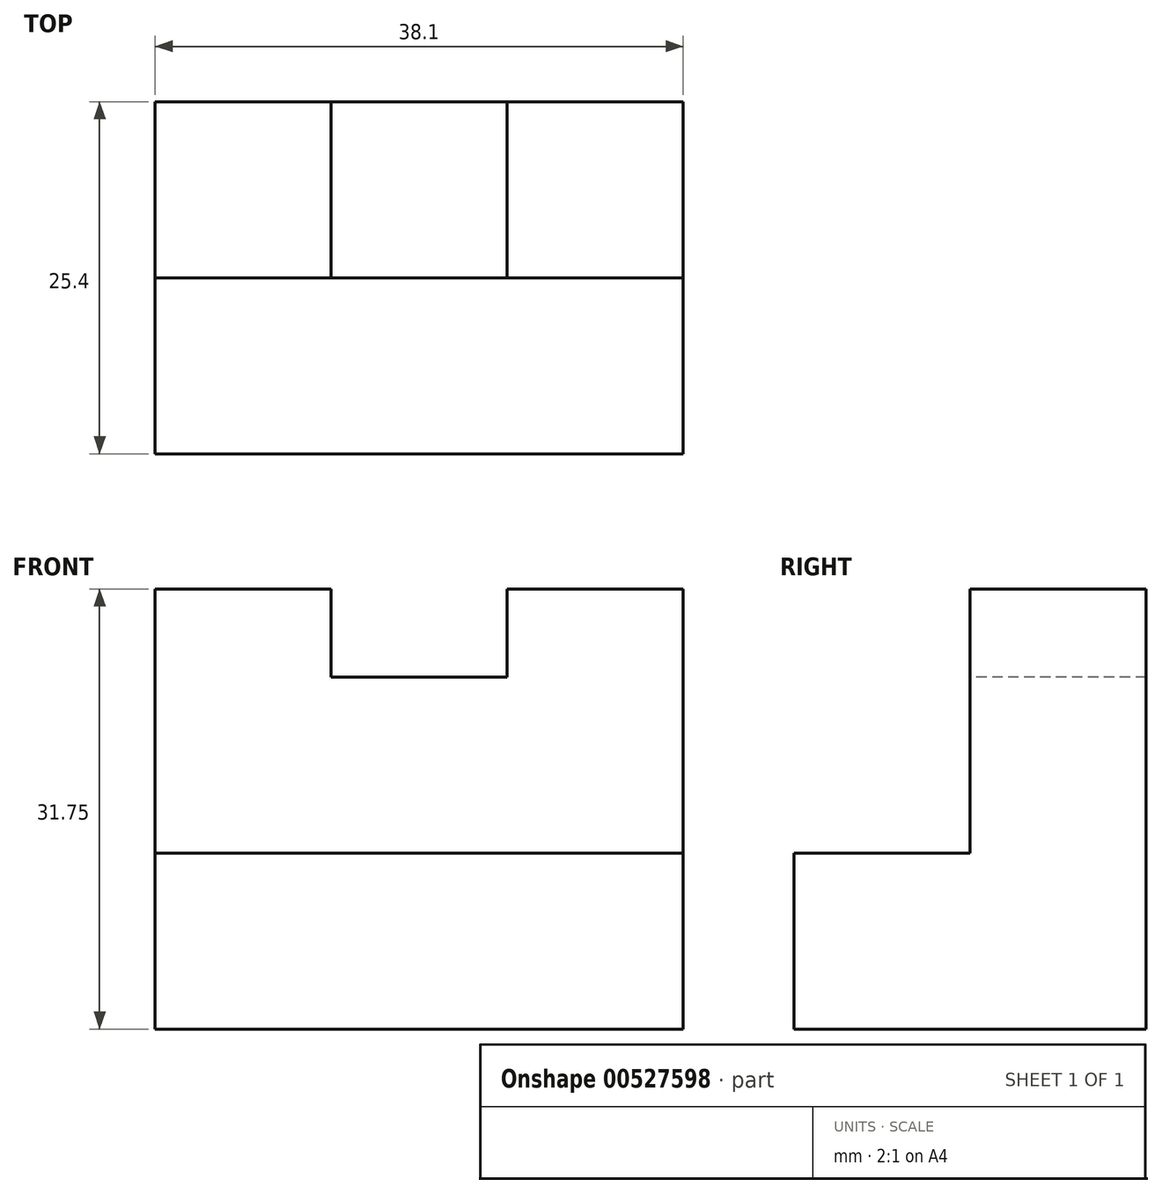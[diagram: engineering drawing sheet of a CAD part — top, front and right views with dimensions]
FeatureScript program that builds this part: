
annotation { "Feature Type Name" : "Feature", "Feature Type Description" : "" }
export const myFeature = defineFeature(function(context is Context, id is Id, definition is map)
    precondition{}
    {
        {
            var Q0;
            Q0=qCreatedBy(makeId("Right.planeOp"),FACE);
            var sketch = newSketch(context, id + "F0", { "sketchPlane" : qUnion([Q0])});
            skLineSegment(sketch, "E0", {"start": v(0, 0) * mm, "end": v(0, 12.7) * mm});
            skLineSegment(sketch, "E1", {"start": v(0, 12.7) * mm, "end": v(12.7, 12.7) * mm});
            skLineSegment(sketch, "E2", {"start": v(12.7, 12.7) * mm, "end": v(12.7, 31.75) * mm});
            skLineSegment(sketch, "E3", {"start": v(12.7, 31.75) * mm, "end": v(25.4, 31.75) * mm});
            skLineSegment(sketch, "E4", {"start": v(25.4, 31.75) * mm, "end": v(25.4, 0) * mm});
            skLineSegment(sketch, "E5", {"start": v(25.4, 0) * mm, "end": v(0, 0) * mm});
            skSolve(sketch);
        }
        {
            var Q0;
            Q0 = qSketchRegion(id + "F0", true);
            extrude(context, id + "F1", {"entities" : qUnion([Q0]), "depth" : 38.1 * mm, "offsetDistance" : 25.4 * mm});
        }
        {
            var Q0;
            Q0=makeQuery(id+"F1.opExtrude","SWEPT_FACE",FACE,{"disambiguationData":[OSD([sQuery(id+"F0.wireOp",EDGE,"E3")])]});
            var sketch = newSketch(context, id + "F2", { "sketchPlane" : qUnion([Q0])});
            skLineSegment(sketch, "E6", {"start": v(0, 25.4) * mm, "end": v(12.7, 25.4) * mm});
            skLineSegment(sketch, "E7", {"start": v(12.7, 25.4) * mm, "end": v(12.7, 12.7) * mm});
            skLineSegment(sketch, "E8", {"start": v(12.7, 25.4) * mm, "end": v(25.38, 25.4) * mm});
            skLineSegment(sketch, "E9", {"start": v(25.38, 25.4) * mm, "end": v(25.38, 12.7) * mm});
            skSolve(sketch);
        }
        {
            var Q0;
            Q0 = qSketchRegion(id + "F2", true);
            var Q1;
            {var subQ0=sQuery(id+"F2.wireOp",EDGE,"E7");Q1=makeQuery(id+"F2.imprint","IMPRINT",FACE,{"disambiguationData":[TD([[makeQuery(id+"F2.imprint","IMPRINT",EDGE,{"derivedFrom":subQ0}),1.0]])]});}
            extrude(context, id + "F3", {"entities" : qUnion([Q0, Q1]), "operationType" : NewBodyOperationType.REMOVE, "oppositeDirection" : true, "depth" : 6.35 * mm, "offsetDistance" : 25.4 * mm});
        }
    });
